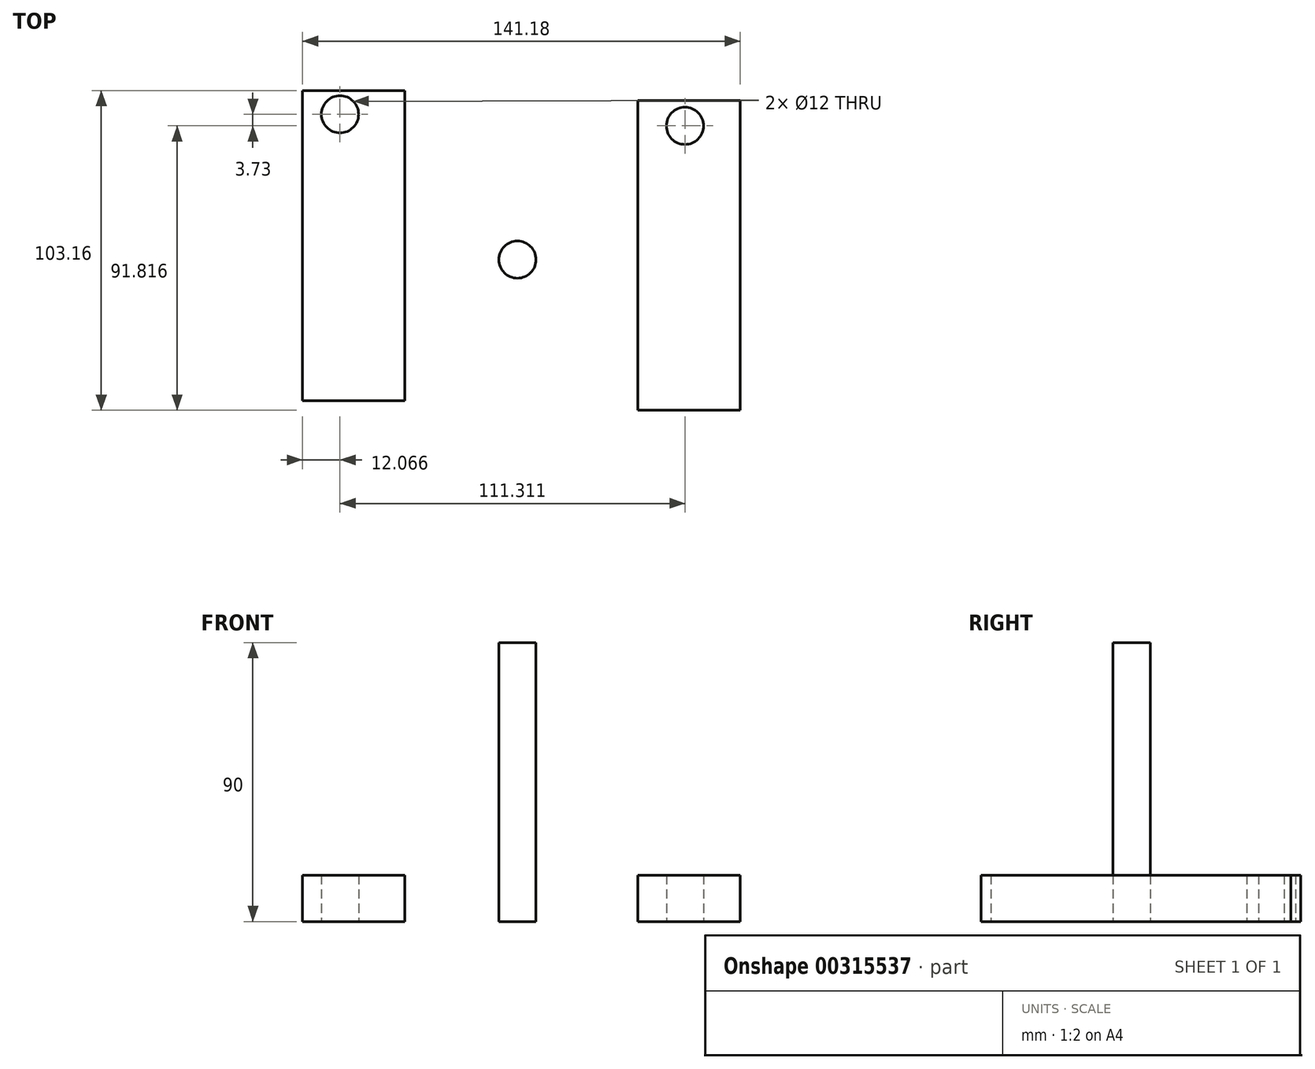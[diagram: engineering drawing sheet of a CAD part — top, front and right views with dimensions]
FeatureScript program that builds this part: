
annotation { "Feature Type Name" : "Feature", "Feature Type Description" : "" }
export const myFeature = defineFeature(function(context is Context, id is Id, definition is map)
    precondition{}
    {
        {
            var Q0;
            Q0=qCreatedBy(makeId("Top.planeOp"),FACE);
            var sketch = newSketch(context, id + "F0", { "sketchPlane" : qUnion([Q0])});
            skCircle(sketch, "E0", {"center": v(0, 0) * mm, "radius": 6 * mm});
            skLineSegment(sketch, "E1.bottom", {"start": v(-69.3, 54.52) * mm, "end": v(-36.3, 54.52) * mm});
            skLineSegment(sketch, "E1.top", {"start": v(-69.3, -45.48) * mm, "end": v(-36.3, -45.48) * mm});
            skLineSegment(sketch, "E1.left", {"start": v(-69.3, 54.52) * mm, "end": v(-69.3, -45.48) * mm});
            skLineSegment(sketch, "E1.right", {"start": v(-36.3, 54.52) * mm, "end": v(-36.3, -45.48) * mm});
            skLineSegment(sketch, "E2.bottom", {"start": v(38.88, 51.36) * mm, "end": v(71.88, 51.36) * mm});
            skLineSegment(sketch, "E2.top", {"start": v(38.88, -48.64) * mm, "end": v(71.88, -48.64) * mm});
            skLineSegment(sketch, "E2.left", {"start": v(38.88, 51.36) * mm, "end": v(38.88, -48.64) * mm});
            skLineSegment(sketch, "E2.right", {"start": v(71.88, 51.36) * mm, "end": v(71.88, -48.64) * mm});
            skCircle(sketch, "E3", {"center": v(-57.23, 46.9) * mm, "radius": 6 * mm});
            skCircle(sketch, "E4", {"center": v(54.08, 43.18) * mm, "radius": 6 * mm});
            skSolve(sketch);
        }
        {
            var Q0;
            Q0=makeQuery(id+"F0.imprint","IMPRINT",FACE,{"disambiguationData":[TD([[makeQuery(id+"F0.imprint","IMPRINT",EDGE,{"derivedFrom":sQuery(id+"F0.wireOp",EDGE,"E1.bottom")}),-1.0]])]});
            var Q1;
            Q1=makeQuery(id+"F0.imprint","IMPRINT",FACE,{"disambiguationData":[TD([[makeQuery(id+"F0.imprint","IMPRINT",EDGE,{"derivedFrom":sQuery(id+"F0.wireOp",EDGE,"E2.bottom")}),-1.0]])]});
            var Q2;
            Q2=makeQuery(id+"F0.imprint","IMPRINT",FACE,{"disambiguationData":[TD([[makeQuery(id+"F0.imprint","IMPRINT",EDGE,{"derivedFrom":sQuery(id+"F0.wireOp",EDGE,"E0")}),1.0]])]});
            extrude(context, id + "F1", {"entities" : qUnion([Q0, Q1, Q2]), "depth" : 15 * mm});
        }
        {
            var Q0;
            Q0=sQuery(id+"F0.wireOp",EDGE,"E0");
            extrude(context, id + "F2", {"bodyType" : ToolBodyType.SURFACE, "surfaceEntities" : qUnion([Q0]), "depth" : 30 * mm});
        }
        {
            var Q0;
            Q0=makeQuery(id+"F1.opExtrude","CAP_FACE",FACE,{"disambiguationData":[OSD([sQuery(id+"F0.wireOp",EDGE,"E0")])],"isStart":false});
            extrude(context, id + "F3", {"entities" : qUnion([Q0]), "operationType" : NewBodyOperationType.ADD, "depth" : 75 * mm});
        }
    });
